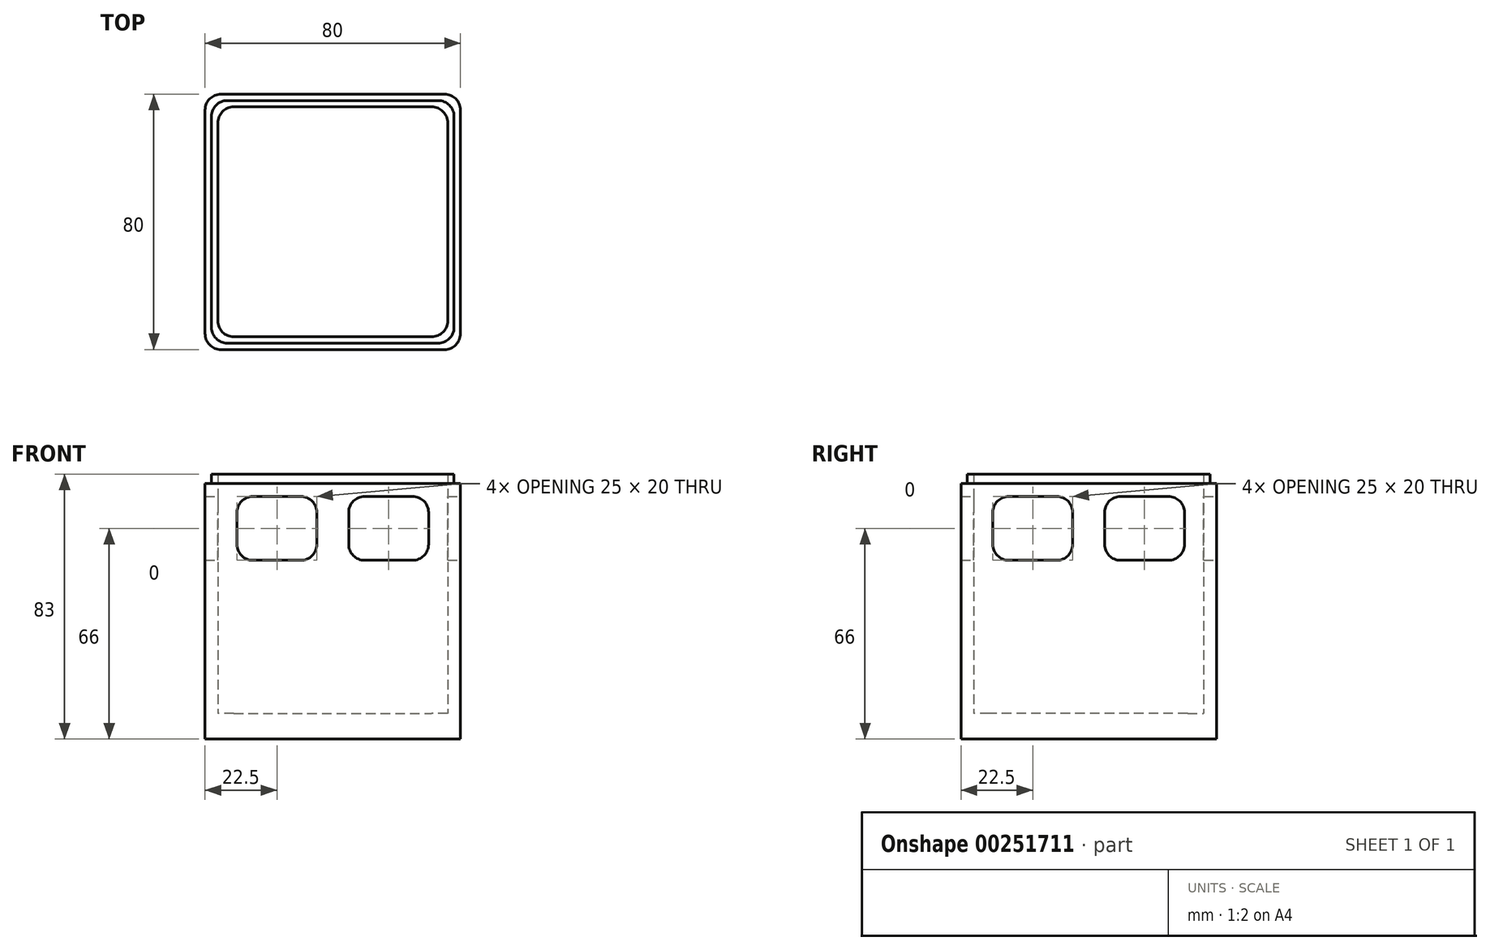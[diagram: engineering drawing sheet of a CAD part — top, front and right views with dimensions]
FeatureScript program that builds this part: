
annotation { "Feature Type Name" : "Feature", "Feature Type Description" : "" }
export const myFeature = defineFeature(function(context is Context, id is Id, definition is map)
    precondition{}
    {
        {
            var Q0;
            Q0=qCreatedBy(makeId("Top.planeOp"),FACE);
            var sketch = newSketch(context, id + "F0", { "sketchPlane" : qUnion([Q0])});
            skLineSegment(sketch, "E0.bottom", {"start": v(-35, 40) * mm, "end": v(35, 40) * mm});
            skLineSegment(sketch, "E0.top", {"start": v(-35, -40) * mm, "end": v(35, -40) * mm});
            skLineSegment(sketch, "E0.left", {"start": v(-40, 35) * mm, "end": v(-40, -35) * mm});
            skLineSegment(sketch, "E0.right", {"start": v(40, 35) * mm, "end": v(40, -35) * mm});
            skPoint(sketch, "E0.middle", {"position": v(0, 0) * mm});
            skLineSegment(sketch, "E1.0", {"start": v(-31, 36) * mm, "end": v(31, 36) * mm});
            skLineSegment(sketch, "E1.1", {"start": v(-36, 31) * mm, "end": v(-36, -31) * mm});
            skLineSegment(sketch, "E1.2", {"start": v(-31, -36) * mm, "end": v(31, -36) * mm});
            skLineSegment(sketch, "E1.3", {"start": v(36, 31) * mm, "end": v(36, -31) * mm});
            skPoint(sketch, "E2.visualSharp", {"position": v(-36, 36) * mm});
            skArc(sketch, "E2.filletArc", {"start": v(-31, 36) * mm, "mid": v(-34.54, 34.54) * mm, "end": v(-36, 31) * mm});
            skPoint(sketch, "E3.visualSharp", {"position": v(-40, 40) * mm});
            skArc(sketch, "E3.filletArc", {"start": v(-35, 40) * mm, "mid": v(-38.54, 38.54) * mm, "end": v(-40, 35) * mm});
            skPoint(sketch, "E4.visualSharp", {"position": v(36, 36) * mm});
            skArc(sketch, "E4.filletArc", {"start": v(36, 31) * mm, "mid": v(34.54, 34.54) * mm, "end": v(31, 36) * mm});
            skPoint(sketch, "E5.visualSharp", {"position": v(40, 40) * mm});
            skArc(sketch, "E5.filletArc", {"start": v(40, 35) * mm, "mid": v(38.54, 38.54) * mm, "end": v(35, 40) * mm});
            skPoint(sketch, "E6.visualSharp", {"position": v(36, -36) * mm});
            skArc(sketch, "E6.filletArc", {"start": v(31, -36) * mm, "mid": v(34.54, -34.54) * mm, "end": v(36, -31) * mm});
            skPoint(sketch, "E7.visualSharp", {"position": v(40, -40) * mm});
            skArc(sketch, "E7.filletArc", {"start": v(35, -40) * mm, "mid": v(38.54, -38.54) * mm, "end": v(40, -35) * mm});
            skPoint(sketch, "E8.visualSharp", {"position": v(-36, -36) * mm});
            skArc(sketch, "E8.filletArc", {"start": v(-36, -31) * mm, "mid": v(-34.54, -34.54) * mm, "end": v(-31, -36) * mm});
            skPoint(sketch, "E9.visualSharp", {"position": v(-40, -40) * mm});
            skArc(sketch, "E9.filletArc", {"start": v(-40, -35) * mm, "mid": v(-38.54, -38.54) * mm, "end": v(-35, -40) * mm});
            skSolve(sketch);
        }
        {
            var Q0;
            Q0=makeQuery(id+"F0.imprint","IMPRINT",FACE,{"disambiguationData":[TD([[makeQuery(id+"F0.imprint","IMPRINT",EDGE,{"derivedFrom":sQuery(id+"F0.wireOp",EDGE,"E0.bottom")}),-1.0]])]});
            extrude(context, id + "F1", {"entities" : qUnion([Q0]), "depth" : 80 * mm});
        }
        {
            var Q0;
            Q0=makeQuery(id+"F0.imprint","IMPRINT",FACE,{"disambiguationData":[TD([[makeQuery(id+"F0.imprint","IMPRINT",EDGE,{"derivedFrom":sQuery(id+"F0.wireOp",EDGE,"E1.0")}),-1.0]])]});
            extrude(context, id + "F2", {"entities" : qUnion([Q0]), "operationType" : NewBodyOperationType.ADD, "depth" : 8 * mm});
        }
        {
            var Q0;
            Q0=makeQuery(id+"F1.opExtrude","CAP_FACE",FACE,{"disambiguationData":[OSD([sQuery(id+"F0.wireOp",EDGE,"E0.bottom"),sQuery(id+"F0.wireOp",EDGE,"E0.top"),sQuery(id+"F0.wireOp",EDGE,"E0.left"),sQuery(id+"F0.wireOp",EDGE,"E0.right"),sQuery(id+"F0.wireOp",EDGE,"E1.0"),sQuery(id+"F0.wireOp",EDGE,"E1.1"),sQuery(id+"F0.wireOp",EDGE,"E1.2"),sQuery(id+"F0.wireOp",EDGE,"E1.3")])],"isStart":false});
            var sketch = newSketch(context, id + "F3", { "sketchPlane" : qUnion([Q0])});
            skLineSegment(sketch, "E10.0", {"start": v(-33, 38) * mm, "end": v(33, 38) * mm});
            skLineSegment(sketch, "E10.1", {"start": v(-38, 33) * mm, "end": v(-38, -33) * mm});
            skLineSegment(sketch, "E10.2", {"start": v(-33, -38) * mm, "end": v(33, -38) * mm});
            skLineSegment(sketch, "E10.3", {"start": v(38, 33) * mm, "end": v(38, -33) * mm});
            skPoint(sketch, "E11.visualSharp", {"position": v(-38, 38) * mm});
            skArc(sketch, "E11.filletArc", {"start": v(-33, 38) * mm, "mid": v(-36.54, 36.54) * mm, "end": v(-38, 33) * mm});
            skPoint(sketch, "E12.visualSharp", {"position": v(38, 38) * mm});
            skArc(sketch, "E12.filletArc", {"start": v(38, 33) * mm, "mid": v(36.54, 36.54) * mm, "end": v(33, 38) * mm});
            skPoint(sketch, "E13.visualSharp", {"position": v(-38, -38) * mm});
            skArc(sketch, "E13.filletArc", {"start": v(-38, -33) * mm, "mid": v(-36.54, -36.54) * mm, "end": v(-33, -38) * mm});
            skPoint(sketch, "E14.visualSharp", {"position": v(38, -38) * mm});
            skArc(sketch, "E14.filletArc", {"start": v(33, -38) * mm, "mid": v(36.54, -36.54) * mm, "end": v(38, -33) * mm});
            skSolve(sketch);
        }
        {
            var Q0;
            Q0=makeQuery(id+"F3.imprint","IMPRINT",FACE,{"disambiguationData":[TD([[makeQuery(id+"F3.imprint","IMPRINT",EDGE,{"derivedFrom":sQuery(id+"F3.wireOp",EDGE,"E10.0")}),-1.0]])]});
            extrude(context, id + "F4", {"entities" : qUnion([Q0]), "operationType" : NewBodyOperationType.ADD, "depth" : 3 * mm});
        }
        {
            var Q0;
            Q0=makeQuery(id+"F1.opExtrude","SWEPT_FACE",FACE,{"disambiguationData":[OSD([sQuery(id+"F0.wireOp",EDGE,"E0.right")])]});
            var sketch = newSketch(context, id + "F5", { "sketchPlane" : qUnion([Q0])});
            skLineSegment(sketch, "E15.0", {"start": v(-35, 80) * mm, "end": v(-35, 0) * mm});
            skLineSegment(sketch, "E16.0", {"start": v(35, 80) * mm, "end": v(35, 0) * mm});
            skLineSegment(sketch, "E17", {"start": v(0, 80) * mm, "end": v(0, 0) * mm});
            skLineSegment(sketch, "E18.bottom", {"start": v(-10, 56) * mm, "end": v(-25, 56) * mm});
            skLineSegment(sketch, "E18.top", {"start": v(-10, 76) * mm, "end": v(-25, 76) * mm});
            skLineSegment(sketch, "E18.left", {"start": v(-5, 61) * mm, "end": v(-5, 71) * mm});
            skLineSegment(sketch, "E18.right", {"start": v(-30, 61) * mm, "end": v(-30, 71) * mm});
            skPoint(sketch, "E18.middle", {"position": v(-17.5, 66) * mm});
            skPoint(sketch, "E19.visualSharp", {"position": v(-30, 76) * mm});
            skArc(sketch, "E19.filletArc", {"start": v(-25, 76) * mm, "mid": v(-28.54, 74.54) * mm, "end": v(-30, 71) * mm});
            skPoint(sketch, "E20.visualSharp", {"position": v(-5, 76) * mm});
            skArc(sketch, "E20.filletArc", {"start": v(-5, 71) * mm, "mid": v(-6.46, 74.54) * mm, "end": v(-10, 76) * mm});
            skPoint(sketch, "E21.visualSharp", {"position": v(-5, 56) * mm});
            skArc(sketch, "E21.filletArc", {"start": v(-10, 56) * mm, "mid": v(-6.46, 57.46) * mm, "end": v(-5, 61) * mm});
            skPoint(sketch, "E22.visualSharp", {"position": v(-30, 56) * mm});
            skArc(sketch, "E22.filletArc", {"start": v(-30, 61) * mm, "mid": v(-28.54, 57.46) * mm, "end": v(-25, 56) * mm});
            skPoint(sketch, "E23.MirrorP", {"position": v(30, 56) * mm});
            skPoint(sketch, "E24.MirrorP", {"position": v(17.5, 66) * mm});
            skLineSegment(sketch, "E25.MirrorCS", {"start": v(10, 56) * mm, "end": v(25, 56) * mm});
            skArc(sketch, "E26.MirrorCS", {"start": v(30, 61) * mm, "mid": v(28.54, 57.46) * mm, "end": v(25, 56) * mm});
            skLineSegment(sketch, "E27.MirrorCS", {"start": v(30, 61) * mm, "end": v(30, 71) * mm});
            skLineSegment(sketch, "E28.MirrorCS", {"start": v(10, 76) * mm, "end": v(25, 76) * mm});
            skPoint(sketch, "E29.MirrorP", {"position": v(30, 76) * mm});
            skPoint(sketch, "E30.MirrorP", {"position": v(5, 56) * mm});
            skArc(sketch, "E31.MirrorCS", {"start": v(5, 71) * mm, "mid": v(6.46, 74.54) * mm, "end": v(10, 76) * mm});
            skArc(sketch, "E32.MirrorCS", {"start": v(25, 76) * mm, "mid": v(28.54, 74.54) * mm, "end": v(30, 71) * mm});
            skPoint(sketch, "E33.MirrorP", {"position": v(5, 76) * mm});
            skLineSegment(sketch, "E34.MirrorCS", {"start": v(5, 61) * mm, "end": v(5, 71) * mm});
            skArc(sketch, "E35.MirrorCS", {"start": v(10, 56) * mm, "mid": v(6.46, 57.46) * mm, "end": v(5, 61) * mm});
            skSolve(sketch);
        }
        {
            var Q0;
            Q0=makeQuery(id+"F1.opExtrude","SWEPT_FACE",FACE,{"disambiguationData":[OSD([sQuery(id+"F0.wireOp",EDGE,"E0.bottom")])]});
            var sketch = newSketch(context, id + "F6", { "sketchPlane" : qUnion([Q0])});
            skLineSegment(sketch, "E36.0", {"start": v(-35, 80) * mm, "end": v(-35, 0) * mm});
            skLineSegment(sketch, "E37.0", {"start": v(35, 80) * mm, "end": v(35, 0) * mm});
            skLineSegment(sketch, "E38", {"start": v(0, 80) * mm, "end": v(0, 0) * mm});
            skLineSegment(sketch, "E39.bottom", {"start": v(-10, 56) * mm, "end": v(-25, 56) * mm});
            skLineSegment(sketch, "E39.top", {"start": v(-10, 76) * mm, "end": v(-25, 76) * mm});
            skLineSegment(sketch, "E39.left", {"start": v(-5, 61) * mm, "end": v(-5, 71) * mm});
            skLineSegment(sketch, "E39.right", {"start": v(-30, 61) * mm, "end": v(-30, 71) * mm});
            skPoint(sketch, "E39.middle", {"position": v(-17.5, 66) * mm});
            skPoint(sketch, "E40.visualSharp", {"position": v(-30, 76) * mm});
            skArc(sketch, "E40.filletArc", {"start": v(-25, 76) * mm, "mid": v(-28.54, 74.54) * mm, "end": v(-30, 71) * mm});
            skPoint(sketch, "E41.visualSharp", {"position": v(-5, 76) * mm});
            skArc(sketch, "E41.filletArc", {"start": v(-5, 71) * mm, "mid": v(-6.46, 74.54) * mm, "end": v(-10, 76) * mm});
            skPoint(sketch, "E42.visualSharp", {"position": v(-5, 56) * mm});
            skArc(sketch, "E42.filletArc", {"start": v(-10, 56) * mm, "mid": v(-6.46, 57.46) * mm, "end": v(-5, 61) * mm});
            skPoint(sketch, "E43.visualSharp", {"position": v(-30, 56) * mm});
            skArc(sketch, "E43.filletArc", {"start": v(-30, 61) * mm, "mid": v(-28.54, 57.46) * mm, "end": v(-25, 56) * mm});
            skPoint(sketch, "E44.MirrorP", {"position": v(30, 56) * mm});
            skPoint(sketch, "E45.MirrorP", {"position": v(17.5, 66) * mm});
            skLineSegment(sketch, "E46.MirrorCS", {"start": v(10, 56) * mm, "end": v(25, 56) * mm});
            skArc(sketch, "E47.MirrorCS", {"start": v(30, 61) * mm, "mid": v(28.54, 57.46) * mm, "end": v(25, 56) * mm});
            skLineSegment(sketch, "E48.MirrorCS", {"start": v(30, 61) * mm, "end": v(30, 71) * mm});
            skLineSegment(sketch, "E49.MirrorCS", {"start": v(10, 76) * mm, "end": v(25, 76) * mm});
            skPoint(sketch, "E50.MirrorP", {"position": v(30, 76) * mm});
            skPoint(sketch, "E51.MirrorP", {"position": v(5, 56) * mm});
            skArc(sketch, "E52.MirrorCS", {"start": v(5, 71) * mm, "mid": v(6.46, 74.54) * mm, "end": v(10, 76) * mm});
            skArc(sketch, "E53.MirrorCS", {"start": v(25, 76) * mm, "mid": v(28.54, 74.54) * mm, "end": v(30, 71) * mm});
            skPoint(sketch, "E54.MirrorP", {"position": v(5, 76) * mm});
            skLineSegment(sketch, "E55.MirrorCS", {"start": v(5, 61) * mm, "end": v(5, 71) * mm});
            skArc(sketch, "E56.MirrorCS", {"start": v(10, 56) * mm, "mid": v(6.46, 57.46) * mm, "end": v(5, 61) * mm});
            skSolve(sketch);
        }
        {
            var Q0;
            Q0=makeQuery(id+"F6.imprint","IMPRINT",FACE,{"disambiguationData":[TD([[makeQuery(id+"F6.imprint","IMPRINT",EDGE,{"derivedFrom":sQuery(id+"F6.wireOp",EDGE,"E39.bottom")}),-1.0]])]});
            var Q1;
            Q1=makeQuery(id+"F6.imprint","IMPRINT",FACE,{"disambiguationData":[TD([[makeQuery(id+"F6.imprint","IMPRINT",EDGE,{"derivedFrom":sQuery(id+"F6.wireOp",EDGE,"E46.MirrorCS")}),1.0]])]});
            extrude(context, id + "F7", {"entities" : qUnion([Q0, Q1]), "operationType" : NewBodyOperationType.REMOVE, "endBound" : BoundingType.THROUGH_ALL, "oppositeDirection" : true, "depth" : 25 * mm});
        }
        {
            var Q0;
            Q0=makeQuery(id+"F5.imprint","IMPRINT",FACE,{"disambiguationData":[TD([[makeQuery(id+"F5.imprint","IMPRINT",EDGE,{"derivedFrom":sQuery(id+"F5.wireOp",EDGE,"E18.bottom")}),-1.0]])]});
            var Q1;
            Q1=makeQuery(id+"F5.imprint","IMPRINT",FACE,{"disambiguationData":[TD([[makeQuery(id+"F5.imprint","IMPRINT",EDGE,{"derivedFrom":sQuery(id+"F5.wireOp",EDGE,"E25.MirrorCS")}),1.0]])]});
            extrude(context, id + "F8", {"entities" : qUnion([Q0, Q1]), "operationType" : NewBodyOperationType.REMOVE, "endBound" : BoundingType.THROUGH_ALL, "oppositeDirection" : true, "depth" : 25 * mm});
        }
    });
